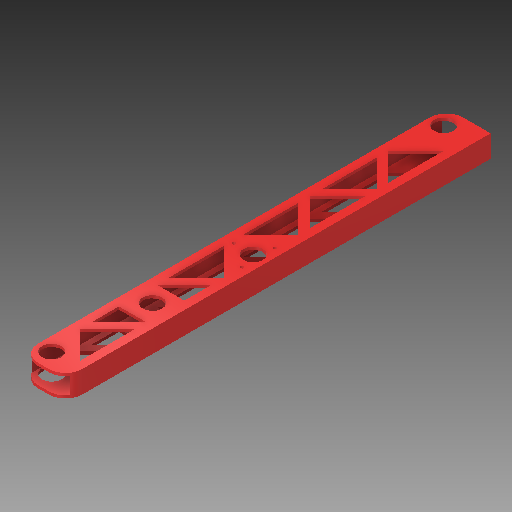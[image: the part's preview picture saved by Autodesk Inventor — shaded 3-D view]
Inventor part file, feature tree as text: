
AUTODESK INVENTOR PART (.ipt)
format: ipt  version: 2017 SP1 (Build 210196100, 196)  size: 229,888 bytes
history: native  units: in
note: dims shown in document units (in); Inventor stores cm internally (conversion verified against a paired STEP export)
features: extrude x3, sketch x3, fillet x1, projected_geometry x1
ambient origin geometry x8: Origin, YZ Plane, XZ Plane, XY Plane, X Axis, Y Axis, Z Axis, Center Point
bodies: Solid1 (feature_tree)
feature tree (8):
  extrude  "Extrusion1"  Depth=2.0in
  extrude  "Extrusion2"  Depth=19.25in TaperAngle=0.0deg
  fillet  "Fillet1"  Radius=0.877in
  extrude  "Extrusion3"  Depth=0.875in TaperAngle=0.0deg
  sketch  "Sketch1"  dims[d0=1.0in d1=2.0in]
  sketch  "Sketch2"  dims[d2=0.125in d3=19.25in d4=0.0in d5=0.877in]
  sketch  "Sketch3"  dims[d10=0.875in d11=20.0in d12=0.0in d13=0.75in d16=0.75in d17=0.625in d20=0.75in d21=0.625in d23=0.625in d24=1.5in d27=1.125in d28=0.15in d29=0.875in d30=0.375in d31=4.201in d32=0.375in d33=1.75in d34=1.0in d35=0.0in d36=0.875in]
  projected_geometry  "Projected Loop1"
